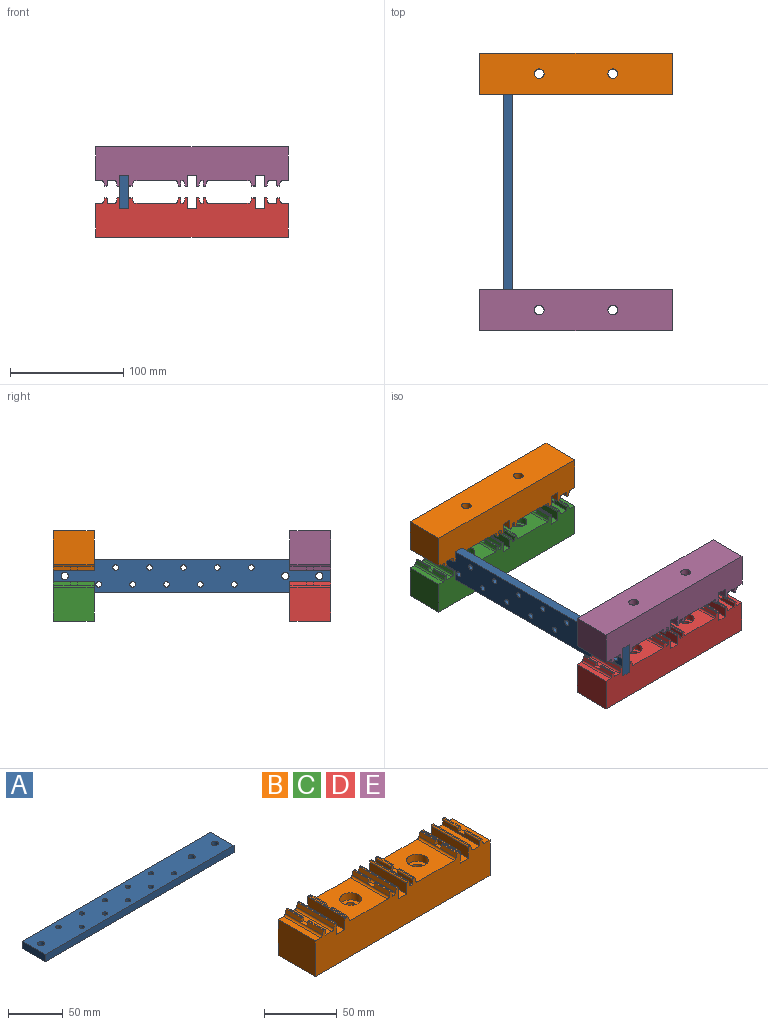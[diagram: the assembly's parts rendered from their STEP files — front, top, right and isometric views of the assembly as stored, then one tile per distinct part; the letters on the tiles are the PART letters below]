
ASSEMBLY  parts=5 mates=7
PART A: 19 faces, bbox 245x30x8 mm
  f0: plane 30x8mm, normal (-1,0,0), area 240mm2, adj f1,f5,f7,f8
  f1: plane 245x8mm, normal (0,-1,0), area 1960mm2, adj f0,f2,f7,f8
  f2: plane 30x8mm, normal (1,0,0), area 240mm2, adj f1,f5,f7,f8
  f3: cylinder r=3.25mm len=8mm, axis (0,0,-1), area 163.4mm2, adj f7,f8
  f4: cylinder r=3.25mm len=8mm, axis (0,0,-1), area 163.4mm2, adj f7,f8
  f5: plane 245x8mm, normal (0,1,0), area 1960mm2, adj f0,f2,f7,f8
  f6: cylinder r=3.25mm len=8mm, axis (0,0,-1), area 163.4mm2, adj f7,f8
  f7: plane 245x30mm, normal (0,0,1), area 7054.1mm2, adj f0,f1,f2,f3,f4,f5,f6,f9
  f8: plane 245x30mm, normal (0,0,-1), area 7054.1mm2, adj f0,f1,f2,f3,f4,f5,f6,f9
  f9: cylinder r=2.5mm len=8mm, axis (0,0,-1), area 125.7mm2, adj f7,f8
  f10: cylinder r=2.5mm len=8mm, axis (0,0,-1), area 125.7mm2, adj f7,f8
  f11: cylinder r=2.5mm len=8mm, axis (0,0,-1), area 125.7mm2, adj f7,f8
  f12: cylinder r=2.5mm len=8mm, axis (0,0,-1), area 125.7mm2, adj f7,f8
  f13: cylinder r=2.5mm len=8mm, axis (0,0,-1), area 125.7mm2, adj f7,f8
  f14: cylinder r=2.5mm len=8mm, axis (0,0,-1), area 125.7mm2, adj f7,f8
  f15: cylinder r=2.5mm len=8mm, axis (0,0,-1), area 125.7mm2, adj f7,f8
  f16: cylinder r=2.5mm len=8mm, axis (0,0,-1), area 125.7mm2, adj f7,f8
  f17: cylinder r=2.5mm len=8mm, axis (0,0,-1), area 125.7mm2, adj f7,f8
  f18: cylinder r=2.5mm len=8mm, axis (0,0,-1), area 125.7mm2, adj f7,f8
PART B: 112 faces, bbox 170x36x35 mm
  f0: plane 36x4mm, normal (-1,0,0), area 129.6mm2, adj f11,f30,f53,f54,f70,f71,f72,f102
  f1: plane 36x4mm, normal (-1,0,0), area 129.6mm2, adj f15,f39,f53,f54,f64,f65,f66,f85
  f2: plane 36x4mm, normal (1,0,0), area 129.6mm2, adj f16,f40,f53,f54,f61,f62,f63,f84
  f3: plane 36x4mm, normal (1,0,0), area 129.6mm2, adj f20,f49,f53,f54,f55,f56,f57,f73
  f4: plane 15x1mm, normal (0,0,1), area 15mm2, adj f10,f11,f54,f72
  f5: plane 15x1mm, normal (0,0,1), area 15mm2, adj f12,f13,f54,f68
  f6: plane 15x1mm, normal (0,0,1), area 15mm2, adj f14,f15,f54,f64
  f7: plane 15x1mm, normal (0,0,1), area 15mm2, adj f40,f42,f53,f63
  f8: plane 15x1mm, normal (0,0,1), area 15mm2, adj f46,f48,f53,f60
  f9: plane 15x1mm, normal (0,0,1), area 15mm2, adj f49,f51,f53,f57
  f10: plane 15x3.4mm, normal (0.96,0,0.28), area 53.2mm2, adj f4,f27,f54,f72
  f11: cylinder r=1mm len=15mm, axis (0,-1,0), area 23.6mm2, adj f0,f4,f54,f72
  f12: cylinder r=1mm len=15mm, axis (0,-1,0), area 23.6mm2, adj f5,f54,f68,f101
  f13: plane 15x3.4mm, normal (-0.96,0,0.28), area 53.2mm2, adj f5,f34,f54,f68
  f14: plane 15x3.4mm, normal (0.96,0,0.28), area 53.2mm2, adj f6,f36,f54,f64
  f15: cylinder r=1mm len=15mm, axis (0,-1,0), area 23.6mm2, adj f1,f6,f54,f64
  f16: cylinder r=1mm len=15mm, axis (0,-1,0), area 23.6mm2, adj f2,f41,f54,f62
  f17: plane 15x3.4mm, normal (-0.96,0,0.28), area 53.2mm2, adj f41,f43,f54,f62
  f18: plane 15x3.4mm, normal (0.96,0,0.28), area 53.2mm2, adj f45,f47,f54,f58
  f19: cylinder r=1mm len=15mm, axis (0,-1,0), area 23.6mm2, adj f47,f54,f58,f74
  f20: cylinder r=1mm len=15mm, axis (0,-1,0), area 23.6mm2, adj f3,f50,f54,f56
  f21: plane 15x3.4mm, normal (-0.96,0,0.28), area 53.2mm2, adj f50,f52,f54,f56
  f22: plane 36x5.4mm, normal (0,0,1), area 194.4mm2, adj f23,f52,f53,f54
  f23: plane 36x30mm, normal (-1,0,0), area 1080mm2, adj f22,f24,f53,f54
  f24: plane 170x36mm, normal (0,0,-1), area 6006.5mm2, adj f23,f25,f53,f54,f106,f109
  f25: plane 36x30mm, normal (1,0,0), area 1080mm2, adj f24,f26,f53,f54
  f26: plane 36x5.4mm, normal (0,0,1), area 194.4mm2, adj f25,f27,f53,f54
  f27: cylinder r=1.6mm len=36mm, axis (0,-1,0), area 90.5mm2, adj f10,f26,f28,f53,f54,f71
  f28: plane 15x3.4mm, normal (0.96,0,0.28), area 53.2mm2, adj f27,f29,f53,f70
  f29: plane 15x1mm, normal (0,0,1), area 15mm2, adj f28,f30,f53,f70
  f30: cylinder r=1mm len=15mm, axis (0,-1,0), area 23.6mm2, adj f0,f29,f53,f70
  f31: cylinder r=1mm len=15mm, axis (0,-1,0), area 23.6mm2, adj f32,f53,f69,f101
  f32: plane 15x1mm, normal (0,0,1), area 15mm2, adj f31,f33,f53,f69
  f33: plane 15x3.4mm, normal (-0.96,0,0.28), area 53.2mm2, adj f32,f34,f53,f69
  f34: cylinder r=1.6mm len=36mm, axis (0,-1,0), area 90.5mm2, adj f13,f33,f35,f53,f54,f67
  f35: plane 36x35.8mm, normal (0,0,1), area 1112.1mm2, adj f34,f36,f53,f54,f111
  f36: cylinder r=1.6mm len=36mm, axis (0,-1,0), area 90.5mm2, adj f14,f35,f37,f53,f54,f65
  f37: plane 15x3.4mm, normal (0.96,0,0.28), area 53.2mm2, adj f36,f38,f53,f66
  f38: plane 15x1mm, normal (0,0,1), area 15mm2, adj f37,f39,f53,f66
  f39: cylinder r=1mm len=15mm, axis (0,-1,0), area 23.6mm2, adj f1,f38,f53,f66
  f40: cylinder r=1mm len=15mm, axis (0,-1,0), area 23.6mm2, adj f2,f7,f53,f63
  f41: plane 15x1mm, normal (0,0,1), area 15mm2, adj f16,f17,f54,f62
  f42: plane 15x3.4mm, normal (-0.96,0,0.28), area 53.2mm2, adj f7,f43,f53,f63
  f43: cylinder r=1.6mm len=36mm, axis (0,-1,0), area 90.5mm2, adj f17,f42,f44,f53,f54,f61
  f44: plane 36x35.8mm, normal (0,0,1), area 1112.1mm2, adj f43,f45,f53,f54,f108
  f45: cylinder r=1.6mm len=36mm, axis (0,-1,0), area 90.5mm2, adj f18,f44,f46,f53,f54,f59
  f46: plane 15x3.4mm, normal (0.96,0,0.28), area 53.2mm2, adj f8,f45,f53,f60
  f47: plane 15x1mm, normal (0,0,1), area 15mm2, adj f18,f19,f54,f58
  f48: cylinder r=1mm len=15mm, axis (0,-1,0), area 23.6mm2, adj f8,f53,f60,f74
  f49: cylinder r=1mm len=15mm, axis (0,-1,0), area 23.6mm2, adj f3,f9,f53,f57
  f50: plane 15x1mm, normal (0,0,1), area 15mm2, adj f20,f21,f54,f56
  f51: plane 15x3.4mm, normal (-0.96,0,0.28), area 53.2mm2, adj f9,f52,f53,f57
  f52: cylinder r=1.6mm len=36mm, axis (0,-1,0), area 90.5mm2, adj f21,f22,f51,f53,f54,f55
  f53: plane 170x35mm, normal (0,1,0), area 5126.3mm2, adj f0,f1,f2,f3,f7,f8,f9,f22
  f54: plane 170x35mm, normal (0,-1,0), area 5126.3mm2, adj f0,f1,f2,f3,f4,f5,f6,f10
  f55: plane 6x3mm, normal (0,0,1), area 18mm2, adj f3,f52,f56,f57
  f56: plane 3.4x3mm, normal (0,1,0), area 8.3mm2, adj f3,f20,f21,f50,f55
  f57: plane 3.4x3mm, normal (0,-1,0), area 8.3mm2, adj f3,f9,f49,f51,f55
  f58: plane 3.4x3mm, normal (0,1,0), area 8.3mm2, adj f18,f19,f47,f59,f74
  f59: plane 6x3mm, normal (0,0,1), area 18mm2, adj f45,f58,f60,f74
  f60: plane 3.4x3mm, normal (0,-1,0), area 8.3mm2, adj f8,f46,f48,f59,f74
  f61: plane 6x3mm, normal (0,0,1), area 18mm2, adj f2,f43,f62,f63
  f62: plane 3.4x3mm, normal (0,1,0), area 8.3mm2, adj f2,f16,f17,f41,f61
  f63: plane 3.4x3mm, normal (0,-1,0), area 8.3mm2, adj f2,f7,f40,f42,f61
  f64: plane 3.4x3mm, normal (0,1,0), area 8.3mm2, adj f1,f6,f14,f15,f65
  f65: plane 6x3mm, normal (0,0,1), area 18mm2, adj f1,f36,f64,f66
  f66: plane 3.4x3mm, normal (0,-1,0), area 8.3mm2, adj f1,f37,f38,f39,f65
  f67: plane 6x3mm, normal (0,0,1), area 18mm2, adj f34,f68,f69,f101
  f68: plane 3.4x3mm, normal (0,1,0), area 8.3mm2, adj f5,f12,f13,f67,f101
  f69: plane 3.4x3mm, normal (0,-1,0), area 8.3mm2, adj f31,f32,f33,f67,f101
  f70: plane 3.4x3mm, normal (0,-1,0), area 8.3mm2, adj f0,f28,f29,f30,f71
  f71: plane 6x3mm, normal (0,0,1), area 18mm2, adj f0,f27,f70,f72
  f72: plane 3.4x3mm, normal (0,1,0), area 8.3mm2, adj f0,f4,f10,f11,f71
  f73: plane 36x6.4mm, normal (0,0,1), area 230.4mm2, adj f3,f53,f54,f80
  f74: plane 36x3.4mm, normal (1,0,0), area 50.4mm2, adj f19,f48,f53,f54,f58,f59,f60,f75
  f75: plane 36x1mm, normal (0,0,1), area 36mm2, adj f53,f54,f74,f76
  f76: plane 36x10mm, normal (-1,0,0), area 360mm2, adj f53,f54,f75,f77
  f77: plane 36x8mm, normal (0,0,1), area 288mm2, adj f53,f54,f76,f78
  f78: plane 36x9mm, normal (1,0,0), area 324mm2, adj f53,f54,f77,f79
  f79: cylinder r=1mm len=36mm, axis (0,-1,0), area 56.5mm2, adj f53,f54,f78,f81
  f80: cylinder r=1.6mm len=36mm, axis (0,-1,0), area 90.5mm2, adj f53,f54,f73,f82
  f81: plane 36x1mm, normal (0,0,1), area 36mm2, adj f53,f54,f79,f82
  f82: plane 36x3.4mm, normal (-0.96,0,0.28), area 127.6mm2, adj f53,f54,f80,f81
  f83: cylinder r=1.6mm len=36mm, axis (0,-1,0), area 90.5mm2, adj f53,f54,f84,f93
  f84: plane 36x1.4mm, normal (0,0,1), area 50.4mm2, adj f2,f53,f54,f83
  f85: plane 36x1.4mm, normal (0,0,1), area 50.4mm2, adj f1,f53,f54,f86
  f86: cylinder r=1.6mm len=36mm, axis (0,-1,0), area 90.5mm2, adj f53,f54,f85,f87
  f87: plane 36x3.4mm, normal (0.96,0,0.28), area 127.6mm2, adj f53,f54,f86,f88
  f88: plane 36x1mm, normal (0,0,1), area 36mm2, adj f53,f54,f87,f89
  f89: cylinder r=1mm len=36mm, axis (0,-1,0), area 56.5mm2, adj f53,f54,f88,f90
  f90: plane 36x9mm, normal (-1,0,0), area 324mm2, adj f53,f54,f89,f91
  f91: plane 36x8mm, normal (0,0,1), area 288mm2, adj f53,f54,f90,f92
  f92: plane 36x9mm, normal (1,0,0), area 324mm2, adj f53,f54,f91,f94
  f93: plane 36x3.4mm, normal (-0.96,0,0.28), area 127.6mm2, adj f53,f54,f83,f95
  f94: cylinder r=1mm len=36mm, axis (0,-1,0), area 56.5mm2, adj f53,f54,f92,f95
  f95: plane 36x1mm, normal (0,0,1), area 36mm2, adj f53,f54,f93,f94
  f96: cylinder r=1mm len=36mm, axis (0,-1,0), area 56.5mm2, adj f53,f54,f97,f105
  f97: plane 36x9mm, normal (-1,0,0), area 324mm2, adj f53,f54,f96,f98
  f98: plane 36x8mm, normal (0,0,1), area 288mm2, adj f53,f54,f97,f99
  f99: plane 36x10mm, normal (1,0,0), area 360mm2, adj f53,f54,f98,f100
  f100: plane 36x1mm, normal (0,0,1), area 36mm2, adj f53,f54,f99,f101
  f101: plane 36x3.4mm, normal (-1,0,0), area 50.4mm2, adj f12,f31,f53,f54,f67,f68,f69,f100
  f102: plane 36x6.4mm, normal (0,0,1), area 230.4mm2, adj f0,f53,f54,f103
  f103: cylinder r=1.6mm len=36mm, axis (0,-1,0), area 90.5mm2, adj f53,f54,f102,f104
  f104: plane 36x3.4mm, normal (0.96,0,0.28), area 127.6mm2, adj f53,f54,f103,f105
  f105: plane 36x1mm, normal (0,0,1), area 36mm2, adj f53,f54,f96,f104
  f106: cylinder r=4.25mm len=24mm, axis (0,0,1), area 640.9mm2, adj f24,f107
  f107: plane 15x15mm, normal (0,0,1), area 120mm2, adj f106,f108
  f108: cylinder r=7.5mm len=15mm, axis (0,0,1), area 282.7mm2, adj f44,f107
  f109: cylinder r=4.25mm len=24mm, axis (0,0,1), area 640.9mm2, adj f24,f110
  f110: plane 15x15mm, normal (0,0,1), area 120mm2, adj f109,f111
  f111: cylinder r=7.5mm len=15mm, axis (0,0,1), area 282.7mm2, adj f35,f110
PART C: same geometry as B
PART D: same geometry as B
PART E: same geometry as B
PLACE A rot(axis=(-0.58,0.58,-0.58),120deg) t=(-281.97,41.33,56.48)mm
PLACE B rot(axis=(-1,0,0),180deg) t=(-217.97,41.33,81.48)mm
PLACE C t=(-217.97,5.33,1.48)mm
PLACE D t=(-217.97,-203.67,1.48)mm
PLACE E rot(axis=(1,0,0),180deg) t=(-217.97,-167.67,81.48)mm
MATE planar E.f53 <-> D.f54  axis (0,-1,0) through (-217.97,-203.67,66.28)mm
MATE planar E.f24 <-> B.f24  axis (0,0,1) through (-217.97,-185.67,81.48)mm
MATE planar D.f54 <-> A.f2  axis (0,-1,0) through (-277.97,-203.67,26.48)mm
MATE parallel A.f0 <-> B.f54  axis (0,1,0) through (-277.97,41.33,56.48)mm
MATE planar D.f25 <-> C.f25  axis (1,0,0) through (-132.97,-185.67,16.48)mm
MATE planar E.f53 <-> A.f2  axis (0,-1,0) through (-277.97,-203.67,56.48)mm
MATE planar C.f53 <-> B.f54  axis (0,1,0) through (-217.97,41.33,16.67)mm
